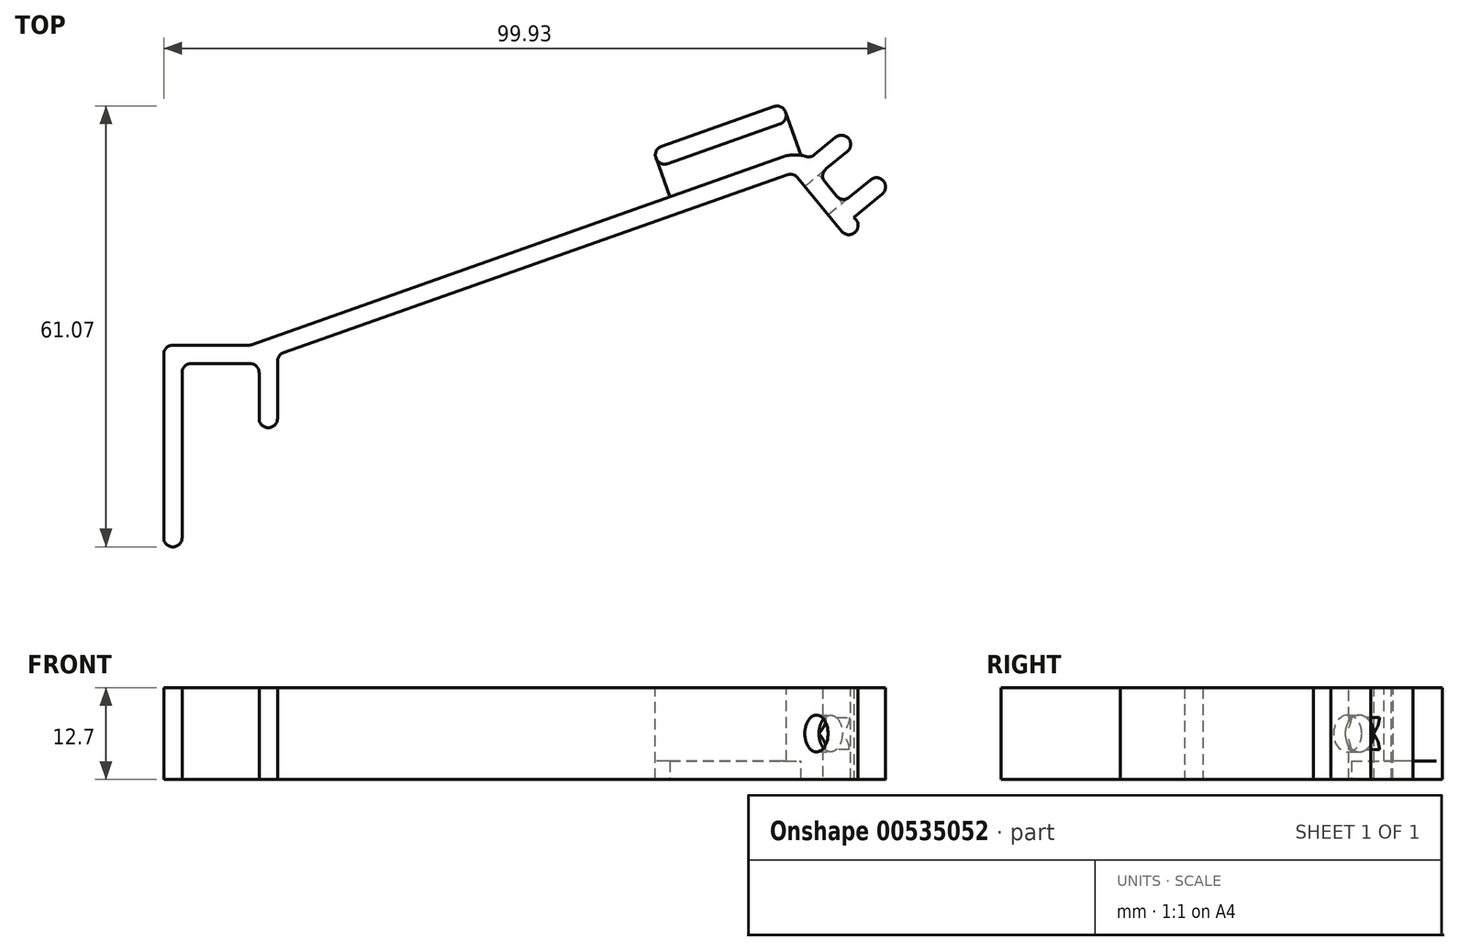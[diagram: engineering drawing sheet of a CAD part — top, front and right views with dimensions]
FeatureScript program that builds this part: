
annotation { "Feature Type Name" : "Feature", "Feature Type Description" : "" }
export const myFeature = defineFeature(function(context is Context, id is Id, definition is map)
    precondition{}
    {
        {
            var Q0;
            Q0=qCreatedBy(makeId("Top.planeOp"),FACE);
            var sketch = newSketch(context, id + "F0", { "sketchPlane" : qUnion([Q0])});
            skLineSegment(sketch, "E0", {"start": v(0, 0) * mm, "end": v(0, 25.4) * mm});
            skLineSegment(sketch, "E1", {"start": v(0, 25.4) * mm, "end": v(10.67, 25.4) * mm});
            skLineSegment(sketch, "E2", {"start": v(10.67, 25.4) * mm, "end": v(10.67, 16.51) * mm});
            skLineSegment(sketch, "E3.0", {"start": v(13.2, 27.94) * mm, "end": v(13.2, 16.51) * mm});
            skLineSegment(sketch, "E3.1", {"start": v(-2.54, 27.94) * mm, "end": v(13.2, 27.94) * mm});
            skLineSegment(sketch, "E3.2", {"start": v(-2.54, 0) * mm, "end": v(-2.54, 27.94) * mm});
            skLineSegment(sketch, "E4", {"start": v(-2.54, 0) * mm, "end": v(0, 0) * mm});
            skLineSegment(sketch, "E5", {"start": v(10.67, 16.51) * mm, "end": v(13.2, 16.51) * mm});
            skLineSegment(sketch, "E6", {"start": v(13.2, 27.94) * mm, "end": v(85.05, 53.34) * mm});
            skLineSegment(sketch, "E7", {"start": v(85.05, 53.34) * mm, "end": v(85.05, 27.94) * mm});
            skLineSegment(sketch, "E8.0", {"start": v(13.2, 26.6) * mm, "end": v(84.63, 51.85) * mm});
            skLineSegment(sketch, "E9.0", {"start": v(9.4, 27.94) * mm, "end": v(85.47, 54.83) * mm});
            skLineSegment(sketch, "E10", {"start": v(85.05, 53.34) * mm, "end": v(93.12, 43.54) * mm});
            skLineSegment(sketch, "E11.0", {"start": v(84.63, 51.85) * mm, "end": v(92.14, 42.73) * mm});
            skLineSegment(sketch, "E12.0", {"start": v(85.47, 54.83) * mm, "end": v(94.1, 44.34) * mm});
            skLineSegment(sketch, "E13", {"start": v(92.14, 42.73) * mm, "end": v(94.1, 44.34) * mm});
            skSolve(sketch);
        }
        {
            var Q0;
            Q0=makeQuery(id+"F0.imprint","IMPRINT",FACE,{"disambiguationData":[TD([[makeQuery(id+"F0.imprint","IMPRINT",EDGE,{"derivedFrom":sQuery(id+"F0.wireOp",EDGE,"E0")}),1.0]])]});
            var Q1;
            {var subQ2=sQuery(id+"F0.wireOp",EDGE,"E6");Q1=makeQuery(id+"F0.imprint","IMPRINT",FACE,{"disambiguationData":[TD([[makeQuery(id+"F0.imprint","IMPRINT",EDGE,{"derivedFrom":subQ2}),1.0]])]});}
            var Q2;
            {var subQ2=sQuery(id+"F0.wireOp",EDGE,"E6");Q2=makeQuery(id+"F0.imprint","IMPRINT",FACE,{"disambiguationData":[TD([[makeQuery(id+"F0.imprint","IMPRINT",EDGE,{"derivedFrom":subQ2}),-1.0]])]});}
            var Q3;
            {var subQ0=sQuery(id+"F0.wireOp",EDGE,"E10");Q3=makeQuery(id+"F0.imprint","IMPRINT",FACE,{"disambiguationData":[TD([[makeQuery(id+"F0.imprint","IMPRINT",EDGE,{"derivedFrom":subQ0}),-1.0]])]});}
            extrude(context, id + "F1", {"entities" : qUnion([Q0, Q1, Q2, Q3]), "depth" : 12.7 * mm, "offsetDistance" : 25.4 * mm});
        }
        {
            var Q0;
            Q0=makeQuery(id+"F1.opExtrude","SWEPT_FACE",FACE,{"disambiguationData":[OSD([sQuery(id+"F0.wireOp",EDGE,"E12.0")])]});
            var sketch = newSketch(context, id + "F2", { "sketchPlane" : qUnion([Q0])});
            skLineSegment(sketch, "E14", {"start": v(-25.6, 12.7) * mm, "end": v(-12, 0) * mm});
            skCircle(sketch, "E15", {"center": v(-18.8, 6.35) * mm, "radius": 2.54 * mm});
            skSolve(sketch);
        }
        {
            var Q0;
            {var subQ0=sQuery(id+"F2.wireOp",EDGE,"E15");var subQ1=sQuery(id+"F2.wireOp",EDGE,"E14");var subQ2=makeQuery(id+"F2.imprint","INTERSECT",VERTEX,{"disambiguationData":[OD(0.0)],"derivedFrom":[subQ1,subQ0]});Q0=makeQuery(id+"F2.imprint","IMPRINT",FACE,{"disambiguationData":[TD([[makeQuery(id+"F2.imprint","IMPRINT",EDGE,{"disambiguationData":[TD([[subQ2,-1.0]])],"derivedFrom":subQ1}),1.0]])]});}
            var Q1;
            {var subQ0=sQuery(id+"F2.wireOp",EDGE,"E15");var subQ1=sQuery(id+"F2.wireOp",EDGE,"E14");var subQ2=makeQuery(id+"F2.imprint","INTERSECT",VERTEX,{"disambiguationData":[OD(0.0)],"derivedFrom":[subQ1,subQ0]});Q1=makeQuery(id+"F2.imprint","IMPRINT",FACE,{"disambiguationData":[TD([[makeQuery(id+"F2.imprint","IMPRINT",EDGE,{"disambiguationData":[TD([[subQ2,-1.0]])],"derivedFrom":subQ1}),-1.0]])]});}
            extrude(context, id + "F3", {"entities" : qUnion([Q0, Q1]), "operationType" : NewBodyOperationType.REMOVE, "oppositeDirection" : true, "depth" : 25.4 * mm, "offsetDistance" : 25.4 * mm});
        }
        {
            var Q0;
            Q0=makeQuery(id+"F1.opExtrude","CAP_FACE",FACE,{"disambiguationData":[OSD([sQuery(id+"F0.wireOp",EDGE,"E0"),sQuery(id+"F0.wireOp",EDGE,"E1"),sQuery(id+"F0.wireOp",EDGE,"E2"),sQuery(id+"F0.wireOp",EDGE,"E3.0"),sQuery(id+"F0.wireOp",EDGE,"E3.1"),sQuery(id+"F0.wireOp",EDGE,"E3.2"),sQuery(id+"F0.wireOp",EDGE,"E4"),sQuery(id+"F0.wireOp",EDGE,"E5"),sQuery(id+"F0.wireOp",EDGE,"E8.0"),sQuery(id+"F0.wireOp",EDGE,"E9.0"),sQuery(id+"F0.wireOp",EDGE,"E11.0"),sQuery(id+"F0.wireOp",EDGE,"E12.0"),sQuery(id+"F0.wireOp",EDGE,"E13")])],"isStart":true});
            var sketch = newSketch(context, id + "F4", { "sketchPlane" : qUnion([Q0])});
            skLineSegment(sketch, "E16", {"start": v(85.47, -54.83) * mm, "end": v(83.98, -59.02) * mm});
            skLineSegment(sketch, "E17", {"start": v(83.98, -59.02) * mm, "end": v(66.02, -52.67) * mm});
            skLineSegment(sketch, "E18", {"start": v(66.02, -52.67) * mm, "end": v(67.5, -48.48) * mm});
            skLineSegment(sketch, "E19.0", {"start": v(83.14, -61.42) * mm, "end": v(65.18, -55.07) * mm});
            skLineSegment(sketch, "E20", {"start": v(83.14, -61.42) * mm, "end": v(83.98, -59.02) * mm});
            skLineSegment(sketch, "E21", {"start": v(66.02, -52.67) * mm, "end": v(65.18, -55.07) * mm});
            skSolve(sketch);
        }
        {
            var Q0;
            Q0=makeQuery(id+"F4.imprint","IMPRINT",FACE,{"disambiguationData":[TD([[makeQuery(id+"F4.imprint","IMPRINT",EDGE,{"derivedFrom":sQuery(id+"F4.wireOp",EDGE,"E17")}),1.0]])]});
            var Q1;
            {var subQ0=sQuery(id+"F4.wireOp",EDGE,"E16");Q1=makeQuery(id+"F4.imprint","IMPRINT",FACE,{"disambiguationData":[TD([[makeQuery(id+"F4.imprint","IMPRINT",EDGE,{"derivedFrom":subQ0}),-1.0]])]});}
            extrude(context, id + "F5", {"entities" : qUnion([Q0, Q1]), "operationType" : NewBodyOperationType.ADD, "oppositeDirection" : true, "depth" : 2.54 * mm, "offsetDistance" : 25.4 * mm});
        }
        {
            var Q0;
            Q0=makeQuery(id+"F4.imprint","IMPRINT",FACE,{"disambiguationData":[TD([[makeQuery(id+"F4.imprint","IMPRINT",EDGE,{"derivedFrom":sQuery(id+"F4.wireOp",EDGE,"E17")}),1.0]])]});
            extrude(context, id + "F6", {"entities" : qUnion([Q0]), "operationType" : NewBodyOperationType.ADD, "oppositeDirection" : true, "depth" : 12.7 * mm, "offsetDistance" : 25.4 * mm});
        }
        {
            var Q0;
            Q0=makeQuery(id+"F1.opExtrude","SWEPT_FACE",FACE,{"disambiguationData":[OSD([sQuery(id+"F0.wireOp",EDGE,"E12.0")])]});
            var sketch = newSketch(context, id + "F7", { "sketchPlane" : qUnion([Q0])});
            skLineSegment(sketch, "E22", {"start": v(-16.26, 12.7) * mm, "end": v(-16.26, 0) * mm});
            skLineSegment(sketch, "E23", {"start": v(-21.34, 12.7) * mm, "end": v(-21.34, 0) * mm});
            skLineSegment(sketch, "E24.0", {"start": v(-13.72, 12.7) * mm, "end": v(-13.72, 0) * mm});
            skLineSegment(sketch, "E25.0", {"start": v(-21.33, 12.7) * mm, "end": v(-21.33, 0) * mm});
            skLineSegment(sketch, "E26.0", {"start": v(-23.87, 12.7) * mm, "end": v(-23.87, 0) * mm});
            skLineSegment(sketch, "E27", {"start": v(-13.72, 12.7) * mm, "end": v(-23.87, 12.7) * mm});
            skLineSegment(sketch, "E28", {"start": v(-23.87, 0) * mm, "end": v(-13.72, 0) * mm});
            skSolve(sketch);
        }
        {
            var Q0;
            {var subQ3=sQuery(id+"F7.wireOp",EDGE,"E24.0");Q0=makeQuery(id+"F7.imprint","IMPRINT",FACE,{"disambiguationData":[TD([[makeQuery(id+"F7.imprint","IMPRINT",EDGE,{"derivedFrom":subQ3}),-1.0]])]});}
            var Q1;
            {var subQ0=sQuery(id+"F7.wireOp",EDGE,"E26.0");Q1=makeQuery(id+"F7.imprint","IMPRINT",FACE,{"disambiguationData":[TD([[makeQuery(id+"F7.imprint","IMPRINT",EDGE,{"derivedFrom":subQ0}),1.0]])]});}
            extrude(context, id + "F8", {"entities" : qUnion([Q0, Q1]), "operationType" : NewBodyOperationType.ADD, "depth" : 6.35 * mm, "offsetDistance" : 25.4 * mm});
        }
        {
            var Q0;
            Q0=makeQuery(id+"F8.opExtrude","CAP_EDGE",EDGE,{"disambiguationData":[OSD([sQuery(id+"F7.wireOp",EDGE,"E26.0")])],"isStart":true});
            var Q1;
            Q1=makeQuery(id+"F8.opExtrude","CAP_EDGE",EDGE,{"disambiguationData":[OSD([sQuery(id+"F7.wireOp",EDGE,"E26.0")])],"isStart":false});
            var Q2;
            Q2=makeQuery(id+"F8.opExtrude","CAP_EDGE",EDGE,{"disambiguationData":[OSD([sQuery(id+"F7.wireOp",EDGE,"E23")])],"isStart":false});
            var Q3;
            Q3=makeQuery(id+"F1.opExtrude","SWEPT_EDGE",EDGE,{"disambiguationData":[OSD([sQuery(id+"F0.wireOp",EDGE,"E11.0"),sQuery(id+"F0.wireOp",EDGE,"E13")])]});
            var Q4;
            {var subQ0=sQuery(id+"F7.wireOp",EDGE,"E23");var subQ1=sQuery(id+"F7.wireOp",EDGE,"E27");Q4=makeQuery(id+"F8.boolean.opBoolean","SPLIT",EDGE,{"disambiguationData":[TD([makeQuery(id+"F8.opExtrude","SWEPT_FACE",FACE,{"disambiguationData":[OSD([subQ1]),TDD([makeQuery(id+"F7.imprint","IMPRINT",EDGE,{"disambiguationData":[TD([[makeQuery(id+"F7.imprint","INTERSECT",VERTEX,{"derivedFrom":[sQuery(id+"F7.wireOp",EDGE,"E22"),subQ1]}),1.0]])],"derivedFrom":subQ1})])]})])],"derivedFrom":makeQuery(id+"F8.opExtrude","CAP_EDGE",EDGE,{"disambiguationData":[OSD([subQ0])],"isStart":true})});}
            var Q5;
            {var subQ0=sQuery(id+"F7.wireOp",EDGE,"E27");var subQ1=sQuery(id+"F7.wireOp",EDGE,"E22");Q5=makeQuery(id+"F8.boolean.opBoolean","SPLIT",EDGE,{"disambiguationData":[TD([makeQuery(id+"F8.opExtrude","SWEPT_FACE",FACE,{"disambiguationData":[OSD([subQ0]),TDD([makeQuery(id+"F7.imprint","IMPRINT",EDGE,{"disambiguationData":[TD([[makeQuery(id+"F7.imprint","INTERSECT",VERTEX,{"derivedFrom":[subQ1,subQ0]}),1.0]])],"derivedFrom":subQ0})])]})])],"derivedFrom":makeQuery(id+"F8.opExtrude","CAP_EDGE",EDGE,{"disambiguationData":[OSD([subQ1])],"isStart":true})});}
            var Q6;
            Q6=makeQuery(id+"F8.opExtrude","CAP_EDGE",EDGE,{"disambiguationData":[OSD([sQuery(id+"F7.wireOp",EDGE,"E22")])],"isStart":false});
            var Q7;
            Q7=makeQuery(id+"F8.opExtrude","CAP_EDGE",EDGE,{"disambiguationData":[OSD([sQuery(id+"F7.wireOp",EDGE,"E24.0")])],"isStart":false});
            var Q8;
            Q8=makeQuery(id+"F8.opExtrude","CAP_EDGE",EDGE,{"disambiguationData":[OSD([sQuery(id+"F7.wireOp",EDGE,"E24.0")])],"isStart":true});
            var Q9;
            {var subQ0=sQuery(id+"F4.wireOp",EDGE,"E20");var subQ1=sQuery(id+"F4.wireOp",EDGE,"E19.0");Q9=makeQuery(id+"F6.boolean.opBoolean","MERGE",EDGE,{"derivedFrom":[makeQuery(id+"F5.opExtrude","SWEPT_EDGE",EDGE,{"disambiguationData":[OSD([subQ1,subQ0])]}),makeQuery(id+"F6.opExtrude","SWEPT_EDGE",EDGE,{"disambiguationData":[OSD([subQ1,subQ0])]})]});}
            var Q10;
            Q10=makeQuery(id+"F6.opExtrude","SWEPT_EDGE",EDGE,{"disambiguationData":[OSD([sQuery(id+"F4.wireOp",EDGE,"E16"),sQuery(id+"F4.wireOp",EDGE,"E17"),sQuery(id+"F4.wireOp",EDGE,"E20")])]});
            var Q11;
            {var subQ0=sQuery(id+"F4.wireOp",EDGE,"E21");var subQ1=sQuery(id+"F4.wireOp",EDGE,"E19.0");Q11=makeQuery(id+"F6.boolean.opBoolean","MERGE",EDGE,{"derivedFrom":[makeQuery(id+"F5.opExtrude","SWEPT_EDGE",EDGE,{"disambiguationData":[OSD([subQ1,subQ0])]}),makeQuery(id+"F6.opExtrude","SWEPT_EDGE",EDGE,{"disambiguationData":[OSD([subQ1,subQ0])]})]});}
            var Q12;
            Q12=makeQuery(id+"F6.opExtrude","SWEPT_EDGE",EDGE,{"disambiguationData":[OSD([sQuery(id+"F4.wireOp",EDGE,"E17"),sQuery(id+"F4.wireOp",EDGE,"E18"),sQuery(id+"F4.wireOp",EDGE,"E21")])]});
            var Q13;
            Q13=makeQuery(id+"F1.opExtrude","SWEPT_EDGE",EDGE,{"disambiguationData":[OSD([sQuery(id+"F0.wireOp",EDGE,"E3.1"),sQuery(id+"F0.wireOp",EDGE,"E9.0")])]});
            var Q14;
            Q14=makeQuery(id+"F1.opExtrude","SWEPT_EDGE",EDGE,{"disambiguationData":[OSD([sQuery(id+"F0.wireOp",EDGE,"E3.1"),sQuery(id+"F0.wireOp",EDGE,"E3.2")])]});
            var Q15;
            Q15=makeQuery(id+"F1.opExtrude","SWEPT_EDGE",EDGE,{"disambiguationData":[OSD([sQuery(id+"F0.wireOp",EDGE,"E3.2"),sQuery(id+"F0.wireOp",EDGE,"E4")])]});
            var Q16;
            Q16=makeQuery(id+"F1.opExtrude","SWEPT_EDGE",EDGE,{"disambiguationData":[OSD([sQuery(id+"F0.wireOp",EDGE,"E0"),sQuery(id+"F0.wireOp",EDGE,"E4")])]});
            var Q17;
            Q17=makeQuery(id+"F1.opExtrude","SWEPT_EDGE",EDGE,{"disambiguationData":[OSD([sQuery(id+"F0.wireOp",EDGE,"E2"),sQuery(id+"F0.wireOp",EDGE,"E5")])]});
            var Q18;
            Q18=makeQuery(id+"F1.opExtrude","SWEPT_EDGE",EDGE,{"disambiguationData":[OSD([sQuery(id+"F0.wireOp",EDGE,"E3.0"),sQuery(id+"F0.wireOp",EDGE,"E5")])]});
            var Q19;
            Q19=makeQuery(id+"F1.opExtrude","SWEPT_EDGE",EDGE,{"disambiguationData":[OSD([sQuery(id+"F0.wireOp",EDGE,"E3.0"),sQuery(id+"F0.wireOp",EDGE,"E8.0")])]});
            var Q20;
            Q20=makeQuery(id+"F1.opExtrude","SWEPT_EDGE",EDGE,{"disambiguationData":[OSD([sQuery(id+"F0.wireOp",EDGE,"E8.0"),sQuery(id+"F0.wireOp",EDGE,"E11.0")])]});
            fillet(context, id + "F9", {"entities" : qUnion([Q0, Q1, Q2, Q3, Q4, Q5, Q6, Q7, Q8, Q9, Q10, Q11, Q12, Q13, Q14, Q15, Q16, Q17, Q18, Q19, Q20]), "radius" : 1.27 * mm, "tangentPropagation" : true, "allowEdgeOverflow" : false});
        }
        {
            var Q0;
            Q0=makeQuery(id+"F5.boolean.opBoolean","SPLIT",EDGE,{"derivedFrom":makeQuery(id+"F1.opExtrude","SWEPT_EDGE",EDGE,{"disambiguationData":[OSD([sQuery(id+"F0.wireOp",EDGE,"E9.0"),sQuery(id+"F0.wireOp",EDGE,"E12.0")])]})});
            fillet(context, id + "F10", {"entities" : qUnion([Q0]), "radius" : 5.08 * mm, "tangentPropagation" : true, "allowEdgeOverflow" : false});
        }
        {
            var Q0;
            Q0=makeQuery(id+"F1.opExtrude","SWEPT_EDGE",EDGE,{"disambiguationData":[OSD([sQuery(id+"F0.wireOp",EDGE,"E12.0"),sQuery(id+"F0.wireOp",EDGE,"E13")])]});
            fillet(context, id + "F11", {"entities" : qUnion([Q0]), "radius" : 1.27 * mm, "tangentPropagation" : true, "allowEdgeOverflow" : false});
        }
        {
            var Q0;
            Q0=makeQuery(id+"F1.opExtrude","SWEPT_EDGE",EDGE,{"disambiguationData":[OSD([sQuery(id+"F0.wireOp",EDGE,"E0"),sQuery(id+"F0.wireOp",EDGE,"E1")])]});
            var Q1;
            Q1=makeQuery(id+"F1.opExtrude","SWEPT_EDGE",EDGE,{"disambiguationData":[OSD([sQuery(id+"F0.wireOp",EDGE,"E1"),sQuery(id+"F0.wireOp",EDGE,"E2")])]});
            fillet(context, id + "F12", {"entities" : qUnion([Q0, Q1]), "radius" : 1.27 * mm, "tangentPropagation" : true, "allowEdgeOverflow" : false});
        }
    });
